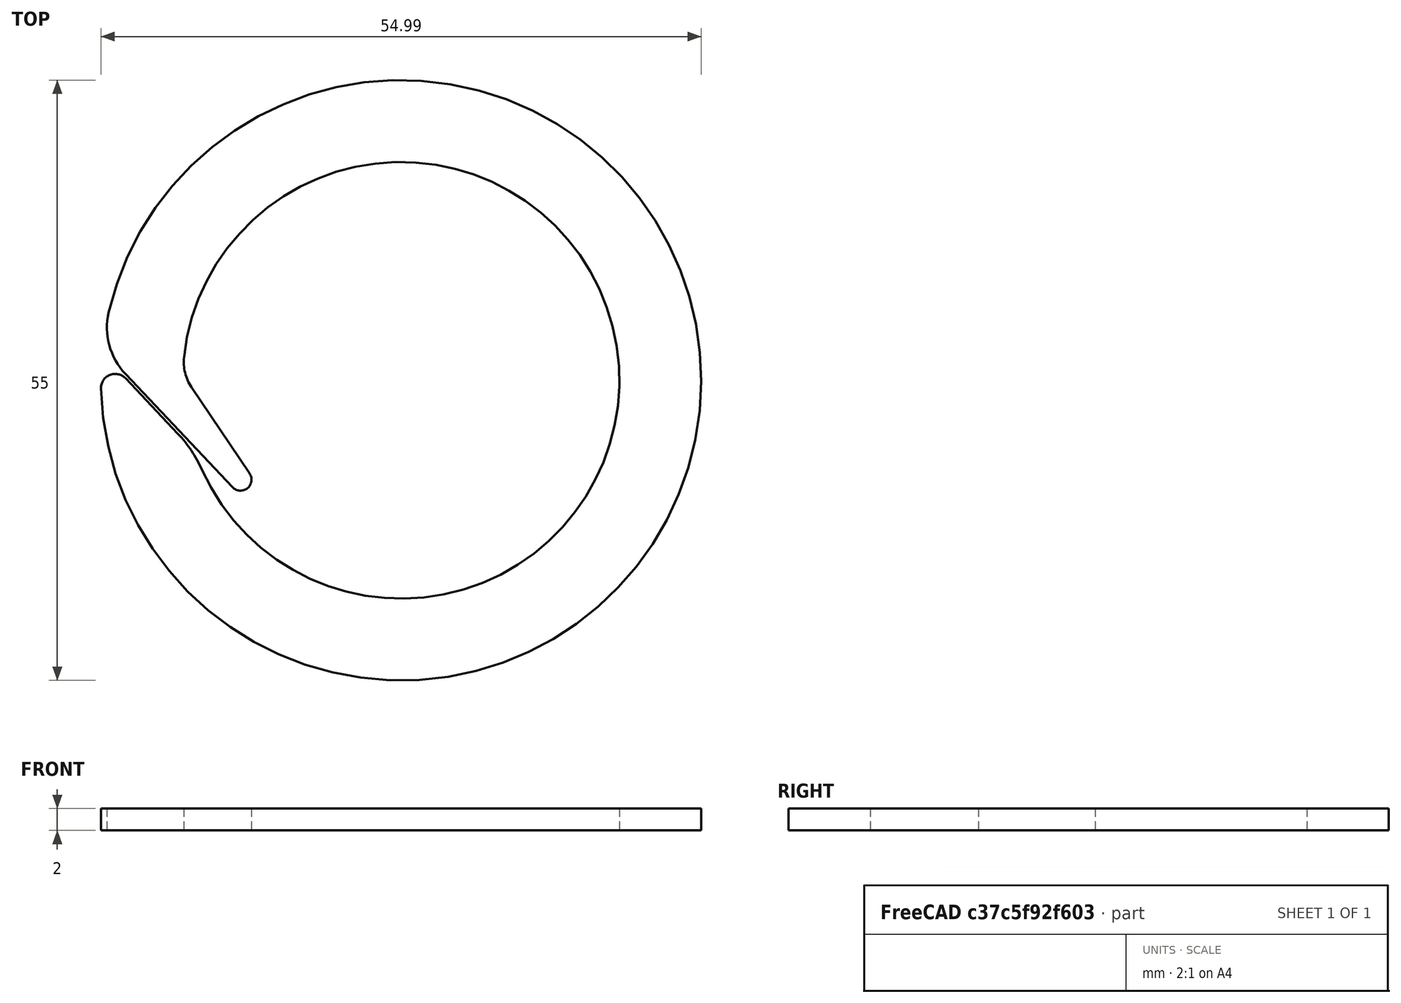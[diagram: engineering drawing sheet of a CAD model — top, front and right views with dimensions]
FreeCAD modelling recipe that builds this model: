
FCSTD DOCUMENT  (FreeCAD 0.22R38261 (Git))
Label: отцеп наконечник
License: All rights reserved
LicenseURL: https://en.wikipedia.org/wiki/All_rights_reserved
objects: Sketcher::SketchObject×1, PartDesign::Pad×1, PartDesign::Body×1, App::Part×1
note: 5 computed .brp shape members not serialized (recipe doc carries the construction recipe); baked Part::Feature solids carry a one-line shape summary decoded from their .brp

FEATURE [Sketcher::SketchObject] Sketch
  AttachmentSupport = -> [XY_Plane001]
  FullyConstrained = false
  MapMode = 5
  sketch-geometry (11):
    g0: ArcOfCircle CenterX=0 CenterY=0 CenterZ=0 NormalX=0 NormalY=0 NormalZ=1 AngleXU=0 Radius=27.5 StartAngle=3.16875 EndAngle=9.19574
    g1: ArcOfCircle CenterX=0 CenterY=0 CenterZ=0 NormalX=0 NormalY=0 NormalZ=1 AngleXU=0 Radius=20 StartAngle=3.56311 EndAngle=9.31855
    g2: LineSegment StartX=-20.4406 StartY=-4.90645 StartZ=0 EndX=-25.2498 EndY=0.179962 EndZ=0
    g3: LineSegment StartX=-25.2498 StartY=0.579962 StartZ=0 EndX=-15.4354 EndY=-9.80013 EndZ=0
    g4: LineSegment StartX=-13.8736 StartY=-8.55085 StartZ=0 EndX=-19.2095 EndY=-0.614914 EndZ=0
    g5: ArcOfCircle CenterX=-14.7063 CenterY=-9.11074 CenterZ=0 NormalX=0 NormalY=0 NormalZ=1 AngleXU=0 Radius=1.00343 StartAngle=3.89899 EndAngle=6.87513
    g6: GeomPoint X=-7.12073 Y=-18.5941 Z=0
    g7: ArcOfCircle CenterX=-26.1927 CenterY=-0.711555 CenterZ=0 NormalX=0 NormalY=0 NormalZ=1 AngleXU=0 Radius=1.29764 StartAngle=0.757393 EndAngle=3.16875
    g8: ArcOfCircle CenterX=-20.7475 CenterY=4.83691 CenterZ=0 NormalX=0 NormalY=0 NormalZ=1 AngleXU=0 Radius=6.19616 StartAngle=2.91255 EndAngle=3.89899
    g9: ArcOfCircle CenterX=-15.7908 CenterY=1.68379 CenterZ=0 NormalX=0 NormalY=0 NormalZ=1 AngleXU=0 Radius=4.11971 StartAngle=3.03536 EndAngle=3.73354
    g10: ArcOfCircle CenterX=-29.0083 CenterY=-13.0072 CenterZ=0 NormalX=0 NormalY=0 NormalZ=1 AngleXU=0 Radius=11.791 StartAngle=0.42152 EndAngle=0.757393
  constraints (22):
    c: Coincident(g1,g-1)
    c: Coincident(g0,g1)
    c: Diameter(g0) = 55
    c: Diameter(g1) = 40  'rvnutr'
    c: PointOnObject(g6,g3)
    c: PointOnObject(g6,g4)
    c: Tangent(g3,g5) = -1.5708
    c: Tangent(g4,g5) = -1.5708
    c: Tangent(g2,g7) = -1.5708
    c: Tangent(g0,g7) = -1.5708
    c: Tangent(g3,g8) = -1.5708
    c: Tangent(g0,g8) = -1.5708
    c: Distance(g2,g3) = 0.4
    c: Parallel(g2,g3)
    c: Vertical(g2,g3)
    c: Tangent(g4,g9) = 1.5708
    c: Tangent(g1,g9) = -1.5708
    c: Tangent(g2,g10) = -1.5708
    c: Tangent(g1,g10) = 1.5708
    c: Distance(g3,g4) = 2
    c: Distance(g2) = 7
    c: Distance(g2,g3) = 7
FEATURE [PartDesign::Pad] Pad
  Direction = (0,0,1)
  Length = 2
  Length2 = 10
  Profile = -> Sketch
  ReferenceAxis = -> Sketch [N_Axis]
  Suppressed = false
  Type = 0
FEATURE [PartDesign::Body] Body
  AllowCompound = false
  Group = -> [Sketch,Pad]
  Origin = -> Origin001
  Tip = -> Pad
FEATURE [App::Part] Part
  Group = -> [Body]
  Origin = -> Origin
